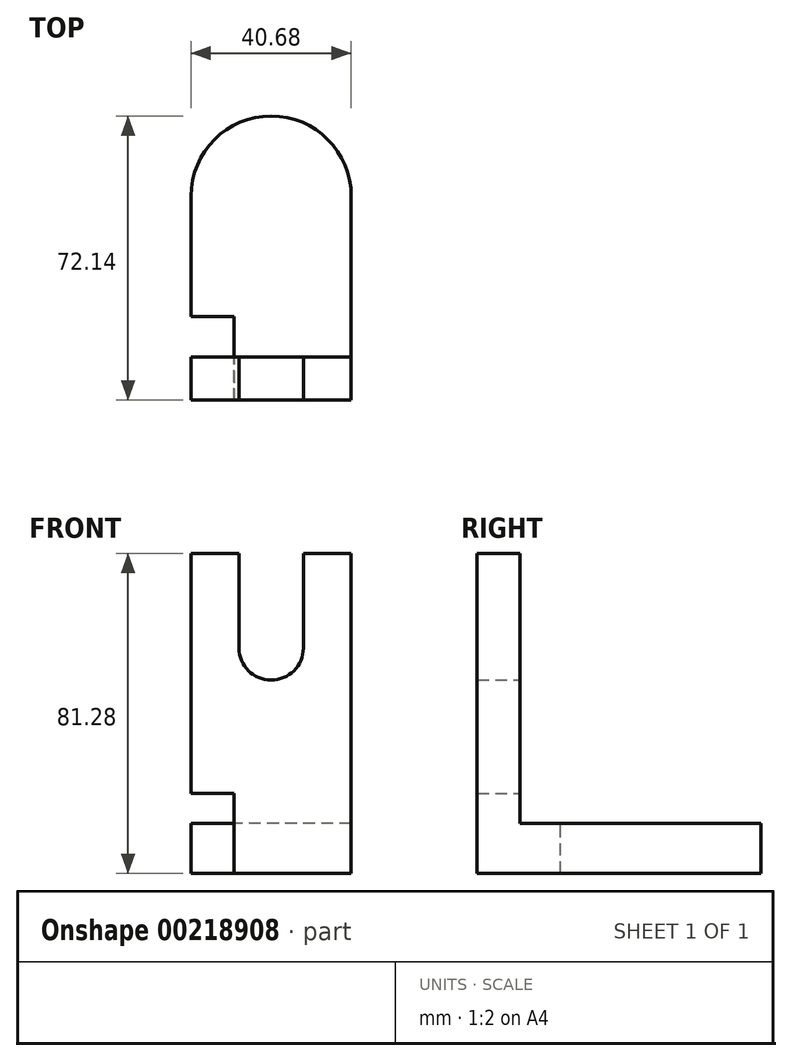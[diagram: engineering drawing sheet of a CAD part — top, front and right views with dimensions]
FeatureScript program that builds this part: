
annotation { "Feature Type Name" : "Feature", "Feature Type Description" : "" }
export const myFeature = defineFeature(function(context is Context, id is Id, definition is map)
    precondition{}
    {
        {
            var Q0;
            Q0=qCreatedBy(makeId("Top.planeOp"),FACE);
            var sketch = newSketch(context, id + "F0", { "sketchPlane" : qUnion([Q0])});
            skLineSegment(sketch, "E0.top", {"start": v(20.34, -25.9) * mm, "end": v(-20.34, -25.9) * mm});
            skLineSegment(sketch, "E0.left", {"start": v(20.34, 25.9) * mm, "end": v(20.34, -25.9) * mm});
            skLineSegment(sketch, "E0.right", {"start": v(-20.34, 25.9) * mm, "end": v(-20.34, -25.9) * mm});
            skPoint(sketch, "E0.middle", {"position": v(0, 0) * mm});
            skArc(sketch, "E1", {"start": v(-20.34, 25.9) * mm, "mid": v(0, 46.24) * mm, "end": v(20.34, 25.9) * mm});
            skSolve(sketch);
        }
        {
            var Q0;
            Q0=makeQuery(id+"F0.imprint","IMPRINT",FACE,{"disambiguationData":[TD([[makeQuery(id+"F0.imprint","IMPRINT",EDGE,{"derivedFrom":sQuery(id+"F0.wireOp",EDGE,"E0.top")}),-1.0]])]});
            extrude(context, id + "F1", {"entities" : qUnion([Q0]), "depth" : 12.7 * mm});
        }
        {
            var Q0;
            Q0=makeQuery(id+"F1.opExtrude","CAP_FACE",FACE,{"disambiguationData":[OSD([sQuery(id+"F0.wireOp",EDGE,"E0.top"),sQuery(id+"F0.wireOp",EDGE,"E0.left"),sQuery(id+"F0.wireOp",EDGE,"E0.right"),sQuery(id+"F0.wireOp",EDGE,"E1")])],"isStart":false});
            var sketch = newSketch(context, id + "F2", { "sketchPlane" : qUnion([Q0])});
            skLineSegment(sketch, "E2.bottom", {"start": v(20.34, -25.9) * mm, "end": v(-20.34, -25.9) * mm});
            skLineSegment(sketch, "E2.top", {"start": v(20.34, -14.97) * mm, "end": v(-20.34, -14.97) * mm});
            skLineSegment(sketch, "E2.left", {"start": v(20.34, -25.9) * mm, "end": v(20.34, -14.97) * mm});
            skLineSegment(sketch, "E2.right", {"start": v(-20.34, -25.9) * mm, "end": v(-20.34, -14.97) * mm});
            skSolve(sketch);
        }
        {
            var Q0;
            Q0=makeQuery(id+"F2.imprint","IMPRINT",FACE,{"disambiguationData":[TD([[makeQuery(id+"F2.imprint","IMPRINT",EDGE,{"derivedFrom":sQuery(id+"F2.wireOp",EDGE,"E2.bottom")}),-1.0]])]});
            extrude(context, id + "F3", {"entities" : qUnion([Q0]), "operationType" : NewBodyOperationType.ADD, "depth" : 68.58 * mm});
        }
        {
            var Q0;
            Q0=makeQuery(id+"F3.opExtrude","SWEPT_FACE",FACE,{"disambiguationData":[OSD([sQuery(id+"F2.wireOp",EDGE,"E2.top")])]});
            var sketch = newSketch(context, id + "F4", { "sketchPlane" : qUnion([Q0])});
            skLineSegment(sketch, "E3.bottom", {"start": v(-8.17, 81.28) * mm, "end": v(8.17, 81.28) * mm});
            skLineSegment(sketch, "E3.left", {"start": v(-8.17, 81.28) * mm, "end": v(-8.17, 57.28) * mm});
            skLineSegment(sketch, "E3.right", {"start": v(8.17, 81.28) * mm, "end": v(8.17, 57.28) * mm});
            skArc(sketch, "E4", {"start": v(-8.17, 57.28) * mm, "mid": v(0, 49.1) * mm, "end": v(8.17, 57.28) * mm});
            skSolve(sketch);
        }
        {
            var Q0;
            Q0=makeQuery(id+"F4.imprint","IMPRINT",FACE,{"disambiguationData":[TD([[makeQuery(id+"F4.imprint","IMPRINT",EDGE,{"derivedFrom":sQuery(id+"F4.wireOp",EDGE,"E3.bottom")}),-1.0]])]});
            extrude(context, id + "F5", {"entities" : qUnion([Q0]), "operationType" : NewBodyOperationType.REMOVE, "oppositeDirection" : true, "depth" : 25.4 * mm});
        }
        {
            var Q0;
            Q0=makeQuery(id+"F3.boolean.opBoolean","MERGE",FACE,{"derivedFrom":[makeQuery(id+"F1.opExtrude","SWEPT_FACE",FACE,{"disambiguationData":[OSD([sQuery(id+"F0.wireOp",EDGE,"E0.right")])]}),makeQuery(id+"F3.opExtrude","SWEPT_FACE",FACE,{"disambiguationData":[OSD([sQuery(id+"F2.wireOp",EDGE,"E2.right")])]})]});
            var sketch = newSketch(context, id + "F6", { "sketchPlane" : qUnion([Q0])});
            skLineSegment(sketch, "E5.bottom", {"start": v(25.9, 0) * mm, "end": v(4.74, 0) * mm});
            skLineSegment(sketch, "E5.top", {"start": v(25.9, 20.31) * mm, "end": v(4.74, 20.31) * mm});
            skLineSegment(sketch, "E5.left", {"start": v(25.9, 0) * mm, "end": v(25.9, 20.31) * mm});
            skLineSegment(sketch, "E5.right", {"start": v(4.74, 0) * mm, "end": v(4.74, 20.31) * mm});
            skSolve(sketch);
        }
        {
            var Q0;
            {var subQ2=sQuery(id+"F6.wireOp",EDGE,"E5.bottom");Q0=makeQuery(id+"F6.imprint","IMPRINT",FACE,{"disambiguationData":[TD([[makeQuery(id+"F6.imprint","IMPRINT",EDGE,{"derivedFrom":subQ2}),1.0]])]});}
            extrude(context, id + "F7", {"entities" : qUnion([Q0]), "operationType" : NewBodyOperationType.REMOVE, "oppositeDirection" : true, "depth" : 10.92 * mm});
        }
    });
